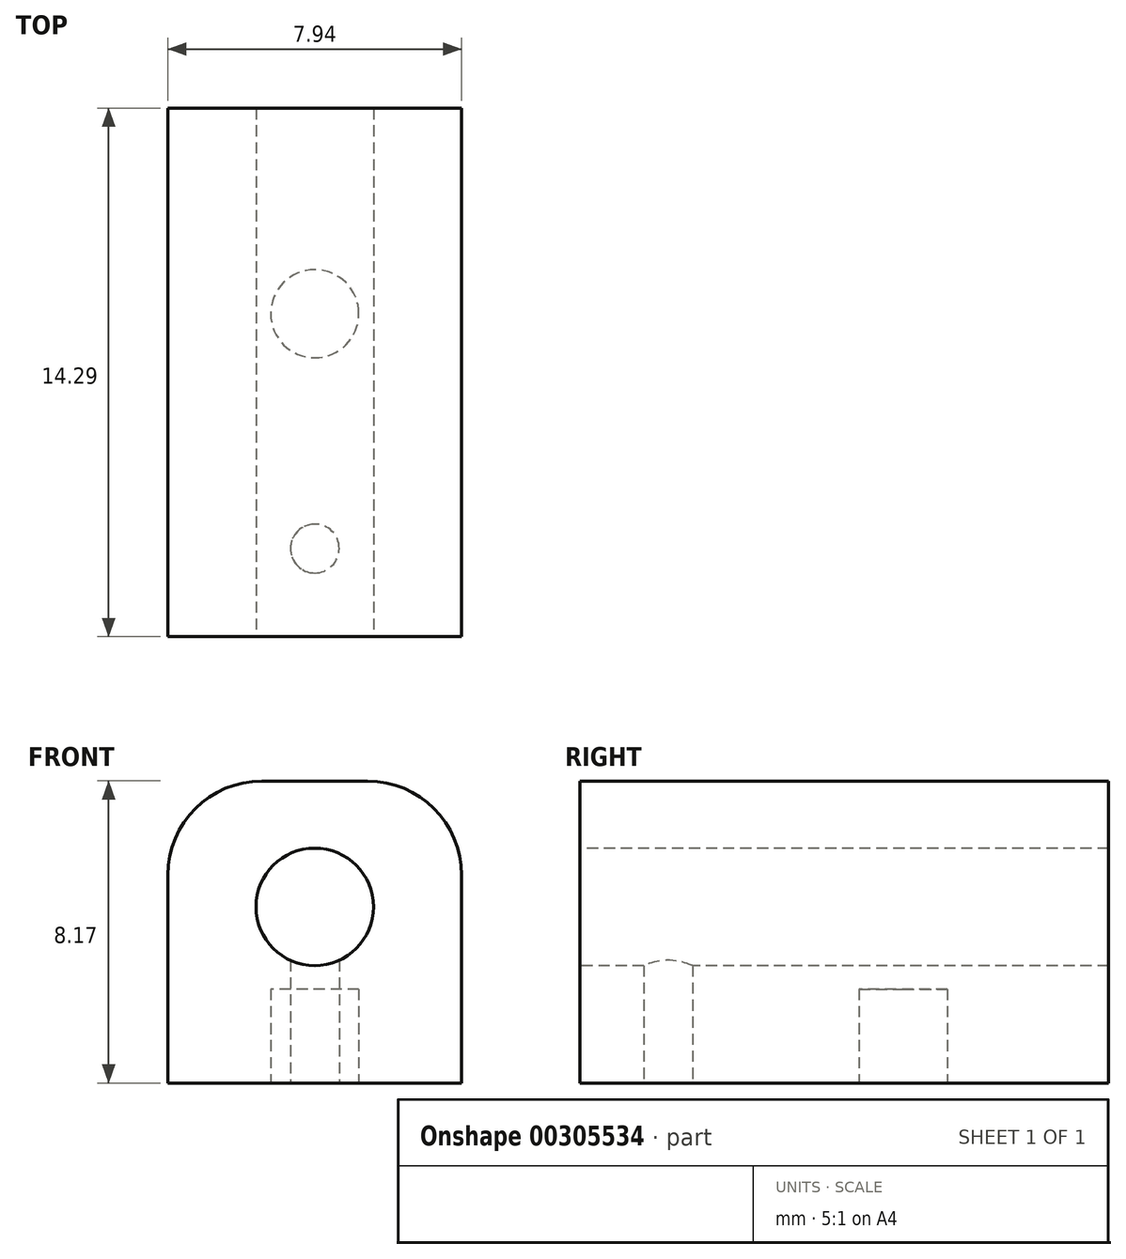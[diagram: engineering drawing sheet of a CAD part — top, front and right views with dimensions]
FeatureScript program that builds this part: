
annotation { "Feature Type Name" : "Feature", "Feature Type Description" : "" }
export const myFeature = defineFeature(function(context is Context, id is Id, definition is map)
    precondition{}
    {
        {
            var Q0;
            Q0=qCreatedBy(makeId("Front.planeOp"),FACE);
            var sketch = newSketch(context, id + "F0", { "sketchPlane" : qUnion([Q0])});
            skLineSegment(sketch, "E0.bottom", {"start": v(0, 0) * mm, "end": v(7.94, 0) * mm});
            skLineSegment(sketch, "E0.top", {"start": v(0, 8.17) * mm, "end": v(7.94, 8.17) * mm});
            skLineSegment(sketch, "E0.left", {"start": v(0, 0) * mm, "end": v(0, 8.17) * mm});
            skLineSegment(sketch, "E0.right", {"start": v(7.94, 0) * mm, "end": v(7.94, 8.17) * mm});
            skLineSegment(sketch, "E1", {"start": v(0, 0) * mm, "end": v(0, -6.35) * mm, "construction": true});
            skLineSegment(sketch, "E2", {"start": v(0, -6.35) * mm, "end": v(3.97, -6.35) * mm, "construction": true});
            skLineSegment(sketch, "E3", {"start": v(3.97, -6.35) * mm, "end": v(3.97, 4.76) * mm, "construction": true});
            skCircle(sketch, "E4", {"center": v(3.97, 4.76) * mm, "radius": 1.59 * mm});
            skSolve(sketch);
        }
        {
            var Q0;
            Q0=makeQuery(id+"F0.imprint","IMPRINT",FACE,{"disambiguationData":[TD([[makeQuery(id+"F0.imprint","IMPRINT",EDGE,{"derivedFrom":sQuery(id+"F0.wireOp",EDGE,"E0.bottom")}),1.0]])]});
            extrude(context, id + "F1", {"entities" : qUnion([Q0]), "oppositeDirection" : true, "depth" : 14.29 * mm});
        }
        {
            var Q0;
            Q0=makeQuery(id+"F1.opExtrude","SWEPT_EDGE",EDGE,{"disambiguationData":[OSD([sQuery(id+"F0.wireOp",EDGE,"E0.top"),sQuery(id+"F0.wireOp",EDGE,"E0.left")])]});
            var Q1;
            Q1=makeQuery(id+"F1.opExtrude","SWEPT_EDGE",EDGE,{"disambiguationData":[OSD([sQuery(id+"F0.wireOp",EDGE,"E0.top"),sQuery(id+"F0.wireOp",EDGE,"E0.right")])]});
            fillet(context, id + "F2", {"entities" : qUnion([Q0, Q1]), "radius" : 2.54 * mm, "tangentPropagation" : true, "allowEdgeOverflow" : false});
        }
        {
            var Q0;
            Q0=qCreatedBy(makeId("Top.planeOp"),FACE);
            var sketch = newSketch(context, id + "F3", { "sketchPlane" : qUnion([Q0])});
            skLineSegment(sketch, "E5", {"start": v(0, 0) * mm, "end": v(3.97, 0) * mm, "construction": true});
            skLineSegment(sketch, "E6", {"start": v(3.97, 0) * mm, "end": v(3.97, 2.38) * mm, "construction": true});
            skLineSegment(sketch, "E7", {"start": v(3.97, 2.38) * mm, "end": v(3.97, 8.73) * mm, "construction": true});
            skCircle(sketch, "E8", {"center": v(3.97, 2.38) * mm, "radius": 0.66 * mm});
            skCircle(sketch, "E9", {"center": v(3.97, 8.73) * mm, "radius": 1.2 * mm});
            skSolve(sketch);
        }
        {
            var Q0;
            Q0=makeQuery(id+"F3.imprint","IMPRINT",FACE,{"disambiguationData":[TD([[makeQuery(id+"F3.imprint","IMPRINT",EDGE,{"derivedFrom":sQuery(id+"F3.wireOp",EDGE,"E9")}),1.0]])]});
            extrude(context, id + "F4", {"entities" : qUnion([Q0]), "operationType" : NewBodyOperationType.REMOVE, "depth" : 2.54 * mm});
        }
        {
            var Q0;
            Q0=makeQuery(id+"F3.imprint","IMPRINT",FACE,{"disambiguationData":[TD([[makeQuery(id+"F3.imprint","IMPRINT",EDGE,{"derivedFrom":sQuery(id+"F3.wireOp",EDGE,"E8")}),1.0]])]});
            extrude(context, id + "F5", {"entities" : qUnion([Q0]), "operationType" : NewBodyOperationType.REMOVE, "depth" : 3.8 * mm});
        }
    });
